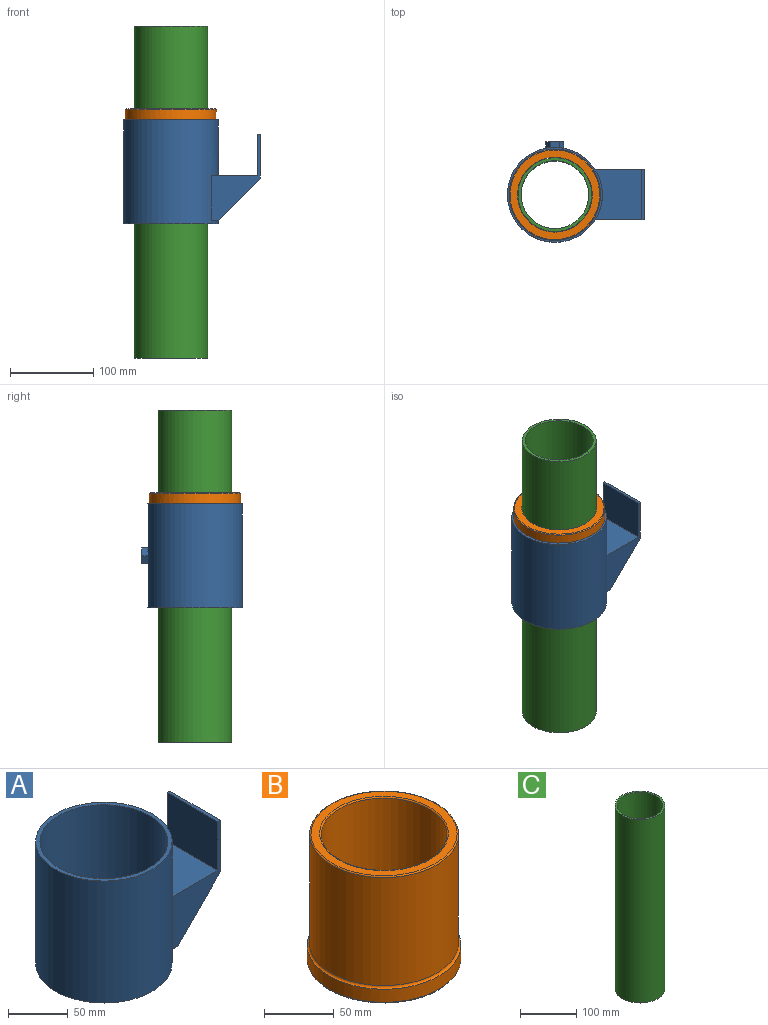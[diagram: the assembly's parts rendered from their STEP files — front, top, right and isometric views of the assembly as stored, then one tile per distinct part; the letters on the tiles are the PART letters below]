
ASSEMBLY  parts=3 mates=4
PART A: 25 faces, bbox 165.1x121.3x125 mm
  f0: plane 60x56.31mm, normal (0,0,1), area 3032.7mm2, adj f1,f14,f16,f23
  f1: cylinder r=57.15mm len=125mm, axis (0,0,-1), area 44033.8mm2, adj f0,f2,f4,f5,f7,f8,f9,f10
  f2: plane 57.58x54mm, normal (0,0,-1), area 2862.2mm2, adj f1,f15,f18,f21
  f3: cylinder r=53.55mm len=125mm, axis (0,0,-1), area 41979.1mm2, adj f4,f5,f6
  f4: plane 114.3x114.3mm, normal (0,0,1), area 1252mm2, adj f1,f3
  f5: plane 114.3x114.3mm, normal (0,0,-1), area 1252mm2, adj f1,f3
  f6: cylinder r=5mm len=10.83mm, axis (0,-1,0), area 336.7mm2, adj f3,f13
  f7: plane 10.91x7.26mm, normal (0,0,-1), area 77.3mm2, adj f1,f9,f12,f13
  f8: plane 10.91x7.26mm, normal (0,0,1), area 77.3mm2, adj f1,f10,f11,f13
  f9: plane 9.48x8.08mm, normal (0.87,0,-0.5), area 83mm2, adj f1,f7,f10,f13
  f10: plane 9.48x8.08mm, normal (0.87,0,0.5), area 83mm2, adj f1,f8,f9,f13
  f11: plane 9.48x8.08mm, normal (-0.87,0,0.5), area 83mm2, adj f1,f8,f12,f13
  f12: plane 9.48x8.08mm, normal (-0.87,0,-0.5), area 83mm2, adj f1,f7,f11,f13
  f13: plane 21.81x18.89mm, normal (0,1,0), area 230.5mm2, adj f6,f7,f8,f9,f10,f11,f12
  f14: plane 103.8x59.31mm, normal (0,-1,0), area 2050.4mm2, adj f0,f1,f15,f20,f22,f23,f24
  f15: plane 60x53mm, normal (1,0,0), area 3180mm2, adj f2,f14,f16,f17,f20,f24
  f16: plane 103.8x59.31mm, normal (0,1,0), area 2050.4mm2, adj f0,f1,f15,f17,f19,f23,f24
  f17: plane 50.8x50.8mm, normal (0.71,0,-0.71), area 215.5mm2, adj f15,f16,f18,f19
  f18: plane 57.58x50.8mm, normal (0,-1,0), area 1634.8mm2, adj f1,f2,f17,f19
  f19: plane 8.51x3mm, normal (0,0,-1), area 22.9mm2, adj f1,f16,f17,f18
  f20: plane 50.8x50.8mm, normal (0.71,0,-0.71), area 215.5mm2, adj f14,f15,f21,f22
  f21: plane 57.58x50.8mm, normal (0,1,0), area 1634.8mm2, adj f1,f2,f20,f22
  f22: plane 8.51x3mm, normal (0,0,-1), area 22.9mm2, adj f1,f14,f20,f21
  f23: plane 60x50mm, normal (-1,0,0), area 3000mm2, adj f0,f14,f16,f24
  f24: plane 60x3mm, normal (0,0,1), area 180mm2, adj f14,f15,f16,f23
PART B: 9 faces, bbox 119.6x119.6x110 mm
  f0: cylinder r=45mm len=109mm, axis (0,0,-1), area 30819mm2, adj f4,f8
  f1: plane 104.5x104.5mm, normal (0,0,1), area 1929.1mm2, adj f6,f8
  f2: cylinder r=53.25mm len=106.5mm, axis (0,0,-1), area 31623mm2, adj f5,f6
  f3: cylinder r=55mm len=110mm, axis (0,0,-1), area 3974.1mm2, adj f5,f7
  f4: plane 108x108mm, normal (0,0,-1), area 2799.2mm2, adj f0,f7
  f5: torus R=55.25mm, axis (0,0,-1), area 978.6mm2, adj f2,f3
  f6: torus R=52.25mm, axis (0,0,-1), area 522mm2, adj f1,f2
  f7: torus R=54mm, axis (0,0,1), area 539.2mm2, adj f3,f4
  f8: torus R=46mm, axis (0,0,-1), area 447.7mm2, adj f0,f1
PART C: 4 faces, bbox 88.9x88.9x400 mm
  f0: cylinder r=40.85mm len=400mm, axis (0,0,-1), area 102667.2mm2, adj f2,f3
  f1: cylinder r=44.45mm len=400mm, axis (0,0,-1), area 111715mm2, adj f2,f3
  f2: plane 88.9x88.9mm, normal (0,0,1), area 964.7mm2, adj f0,f1
  f3: plane 88.9x88.9mm, normal (0,0,-1), area 964.7mm2, adj f0,f1
PLACE A t=(121.42,16.81,161.84)mm
PLACE B rot(axis=(1,0,0),180deg) t=(121.42,16.81,300)mm
PLACE C t=(121.42,16.81,0)mm
MATE planar A.f1 <-> B.f0  axis (0,0,1) through (121.42,16.81,286.84)mm
MATE cylindrical A.f3 <-> B.f0  axis (0,0,-1) through (121.42,16.81,286.84)mm
MATE cylindrical B.f0 <-> C.f1  axis (0,0,1) through (121.42,16.81,238.26)mm
MATE planar C.f1 <-> B.f0  axis (0,0,1) through (121.42,16.81,400)mm
